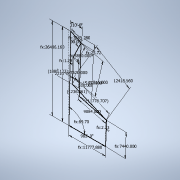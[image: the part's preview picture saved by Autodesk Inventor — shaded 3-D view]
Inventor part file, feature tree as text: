
AUTODESK INVENTOR PART (.ipt)
format: ipt  version: 2021 (Build 250183000, 183)  size: 116,224 bytes
history: native  units: in
note: dims shown in document units (in); Inventor stores cm internally (conversion verified against a paired STEP export)
features: sketch x1
ambient origin geometry x8: Origin, YZ Plane, XZ Plane, XY Plane, X Axis, Y Axis, Z Axis, Center Point
feature tree (1):
  sketch  "Sketch1"  dims[d0=26520.0in d1=11784.0in d2=0.0088in d3=26486.16in d4=11777.88in d5=0.6164in d6=3720.0in d7=0.1767in d8=90.0deg d9=5880.0in d10=7620.0in d12=7440.0in d13=0.0153in d16=3665.28in d17=11778.7072in d22=15132.0in d23=9084.0in d24=100.0in d25=11316.0in d27=12418.56in d29=1236.8611in d30=1880.123in]
